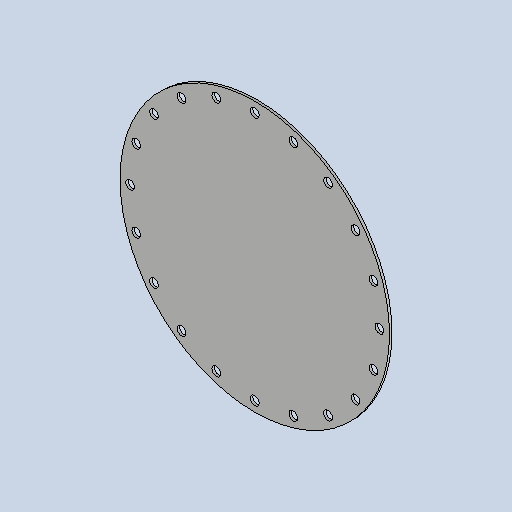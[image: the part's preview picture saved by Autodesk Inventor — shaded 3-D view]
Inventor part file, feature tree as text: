
AUTODESK INVENTOR PART (.ipt)
format: ipt  version: 2025.1 (Build 291241020, 241B)  size: 203,264 bytes
history: native  units: mm
features: sketch x2, other x2, extrude x1, pattern_circular x1
ambient origin geometry x8: Origin, YZ Plane, XZ Plane, XY Plane, X Axis, Y Axis, Z Axis, Center Point
bodies: Solid1 (feature_tree)
feature tree (6):
  extrude  "Extrusion1"  Depth=6.0mm TaperAngle=0.0deg
  pattern_circular  "Circular Pattern1"  Count=62  [1 undecoded]
  sketch  "Sketch1"  dims[d0=670.0mm d1=6.0mm d2=0.0mm]
  sketch  "Sketch2"  dims[d3=22.0mm d4=620.0mm d5=6.0mm d6=6.0mm d7=0.0mm d8=200.0mm d9=360.0deg]
  other  "Cut1"
  other  "Definition1"
note: 1 required parameter value undecoded (feature->parameter linkage not recoverable at this tier; creation-order binding heuristic only, values carry confidence <= 0.55)
